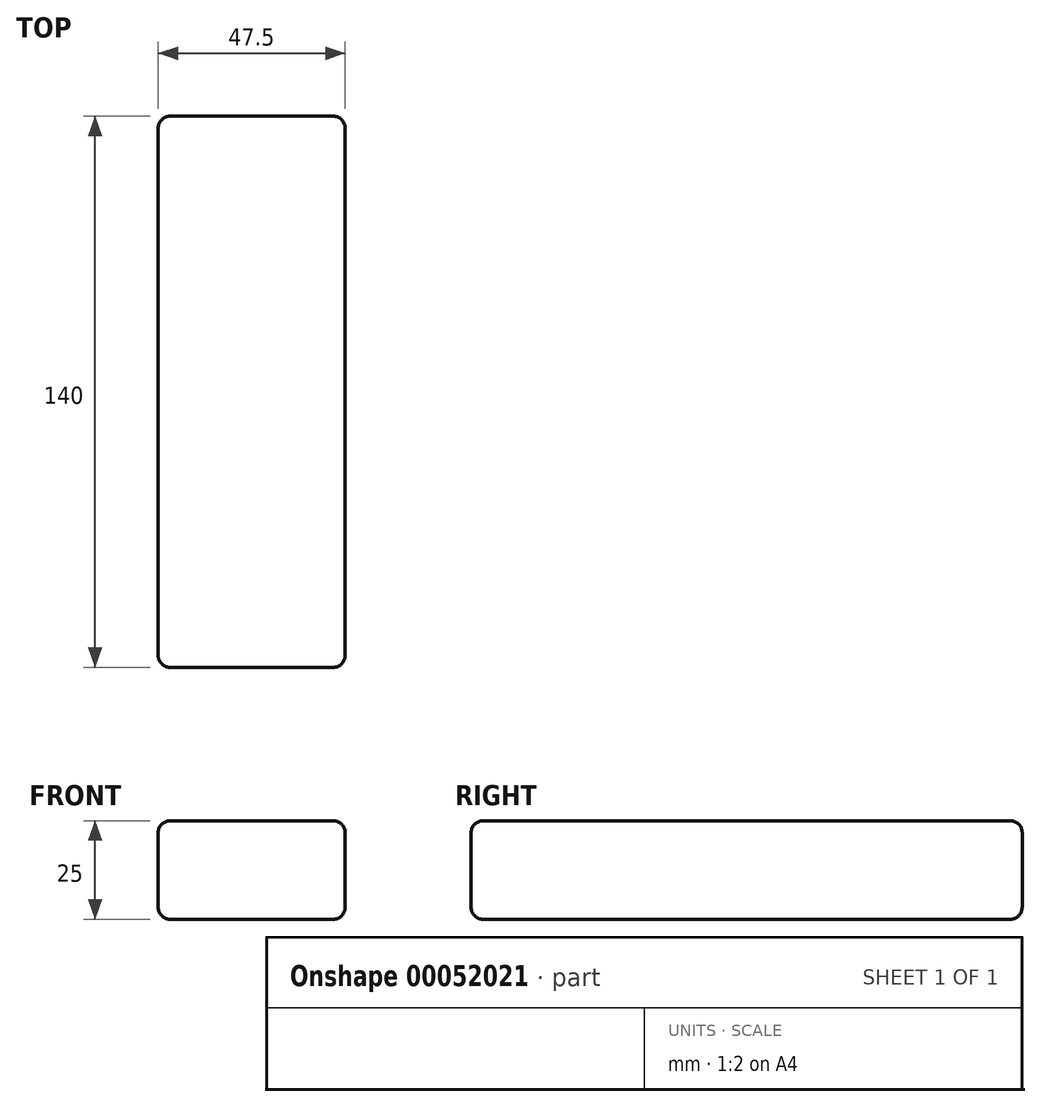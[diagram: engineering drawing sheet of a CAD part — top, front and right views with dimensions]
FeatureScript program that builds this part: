
annotation { "Feature Type Name" : "Feature", "Feature Type Description" : "" }
export const myFeature = defineFeature(function(context is Context, id is Id, definition is map)
    precondition{}
    {
        {
            var Q0;
            Q0=qCreatedBy(makeId("Top.planeOp"),FACE);
            var sketch = newSketch(context, id + "F0", { "sketchPlane" : qUnion([Q0])});
            skLineSegment(sketch, "E0.bottom", {"start": v(-23.75, 70) * mm, "end": v(23.75, 70) * mm});
            skLineSegment(sketch, "E0.top", {"start": v(-23.75, -70) * mm, "end": v(23.75, -70) * mm});
            skLineSegment(sketch, "E0.left", {"start": v(-23.75, 70) * mm, "end": v(-23.75, -70) * mm});
            skLineSegment(sketch, "E0.right", {"start": v(23.75, 70) * mm, "end": v(23.75, -70) * mm});
            skLineSegment(sketch, "E1", {"start": v(-23.75, 70) * mm, "end": v(23.75, -70) * mm});
            skPoint(sketch, "E2", {"position": v(0, 0) * mm});
            skSolve(sketch);
        }
        {
            var Q0;
            Q0=makeQuery(id+"F0.imprint","IMPRINT",FACE,{"disambiguationData":[TD([[makeQuery(id+"F0.imprint","IMPRINT",EDGE,{"derivedFrom":sQuery(id+"F0.wireOp",EDGE,"E0.bottom")}),-1.0]])]});
            var Q1;
            Q1=makeQuery(id+"F0.imprint","IMPRINT",FACE,{"disambiguationData":[TD([[makeQuery(id+"F0.imprint","IMPRINT",EDGE,{"derivedFrom":sQuery(id+"F0.wireOp",EDGE,"E0.top")}),1.0]])]});
            extrude(context, id + "F1", {"entities" : qUnion([Q0, Q1]), "endBound" : BoundingType.SYMMETRIC, "depth" : 25 * mm});
        }
        {
            var Q0;
            Q0=makeQuery(id+"F1.opExtrude","CAP_EDGE",EDGE,{"disambiguationData":[OSD([sQuery(id+"F0.wireOp",EDGE,"E0.left")])],"isStart":false});
            var Q1;
            Q1=makeQuery(id+"F1.opExtrude","CAP_EDGE",EDGE,{"disambiguationData":[OSD([sQuery(id+"F0.wireOp",EDGE,"E0.left")])],"isStart":true});
            var Q2;
            Q2=makeQuery(id+"F1.opExtrude","CAP_EDGE",EDGE,{"disambiguationData":[OSD([sQuery(id+"F0.wireOp",EDGE,"E0.right")])],"isStart":false});
            var Q3;
            Q3=makeQuery(id+"F1.opExtrude","CAP_EDGE",EDGE,{"disambiguationData":[OSD([sQuery(id+"F0.wireOp",EDGE,"E0.bottom")])],"isStart":false});
            var Q4;
            Q4=makeQuery(id+"F1.opExtrude","CAP_EDGE",EDGE,{"disambiguationData":[OSD([sQuery(id+"F0.wireOp",EDGE,"E0.top")])],"isStart":false});
            var Q5;
            Q5=makeQuery(id+"F1.opExtrude","SWEPT_EDGE",EDGE,{"disambiguationData":[OSD([sQuery(id+"F0.wireOp",EDGE,"E0.bottom"),sQuery(id+"F0.wireOp",EDGE,"E0.left"),sQuery(id+"F0.wireOp",EDGE,"E1")])]});
            var Q6;
            Q6=makeQuery(id+"F1.opExtrude","SWEPT_EDGE",EDGE,{"disambiguationData":[OSD([sQuery(id+"F0.wireOp",EDGE,"E0.top"),sQuery(id+"F0.wireOp",EDGE,"E0.left")])]});
            var Q7;
            Q7=makeQuery(id+"F1.opExtrude","CAP_EDGE",EDGE,{"disambiguationData":[OSD([sQuery(id+"F0.wireOp",EDGE,"E0.bottom")])],"isStart":true});
            var Q8;
            Q8=makeQuery(id+"F1.opExtrude","SWEPT_EDGE",EDGE,{"disambiguationData":[OSD([sQuery(id+"F0.wireOp",EDGE,"E0.bottom"),sQuery(id+"F0.wireOp",EDGE,"E0.right")])]});
            var Q9;
            Q9=makeQuery(id+"F1.opExtrude","CAP_EDGE",EDGE,{"disambiguationData":[OSD([sQuery(id+"F0.wireOp",EDGE,"E0.right")])],"isStart":true});
            var Q10;
            Q10=makeQuery(id+"F1.opExtrude","CAP_EDGE",EDGE,{"disambiguationData":[OSD([sQuery(id+"F0.wireOp",EDGE,"E0.top")])],"isStart":true});
            var Q11;
            Q11=makeQuery(id+"F1.opExtrude","SWEPT_EDGE",EDGE,{"disambiguationData":[OSD([sQuery(id+"F0.wireOp",EDGE,"E0.top"),sQuery(id+"F0.wireOp",EDGE,"E0.right"),sQuery(id+"F0.wireOp",EDGE,"E1")])]});
            fillet(context, id + "F2", {"entities" : qUnion([Q0, Q1, Q2, Q3, Q4, Q5, Q6, Q7, Q8, Q9, Q10, Q11]), "radius" : 3 * mm, "tangentPropagation" : true, "allowEdgeOverflow" : false});
        }
    });
